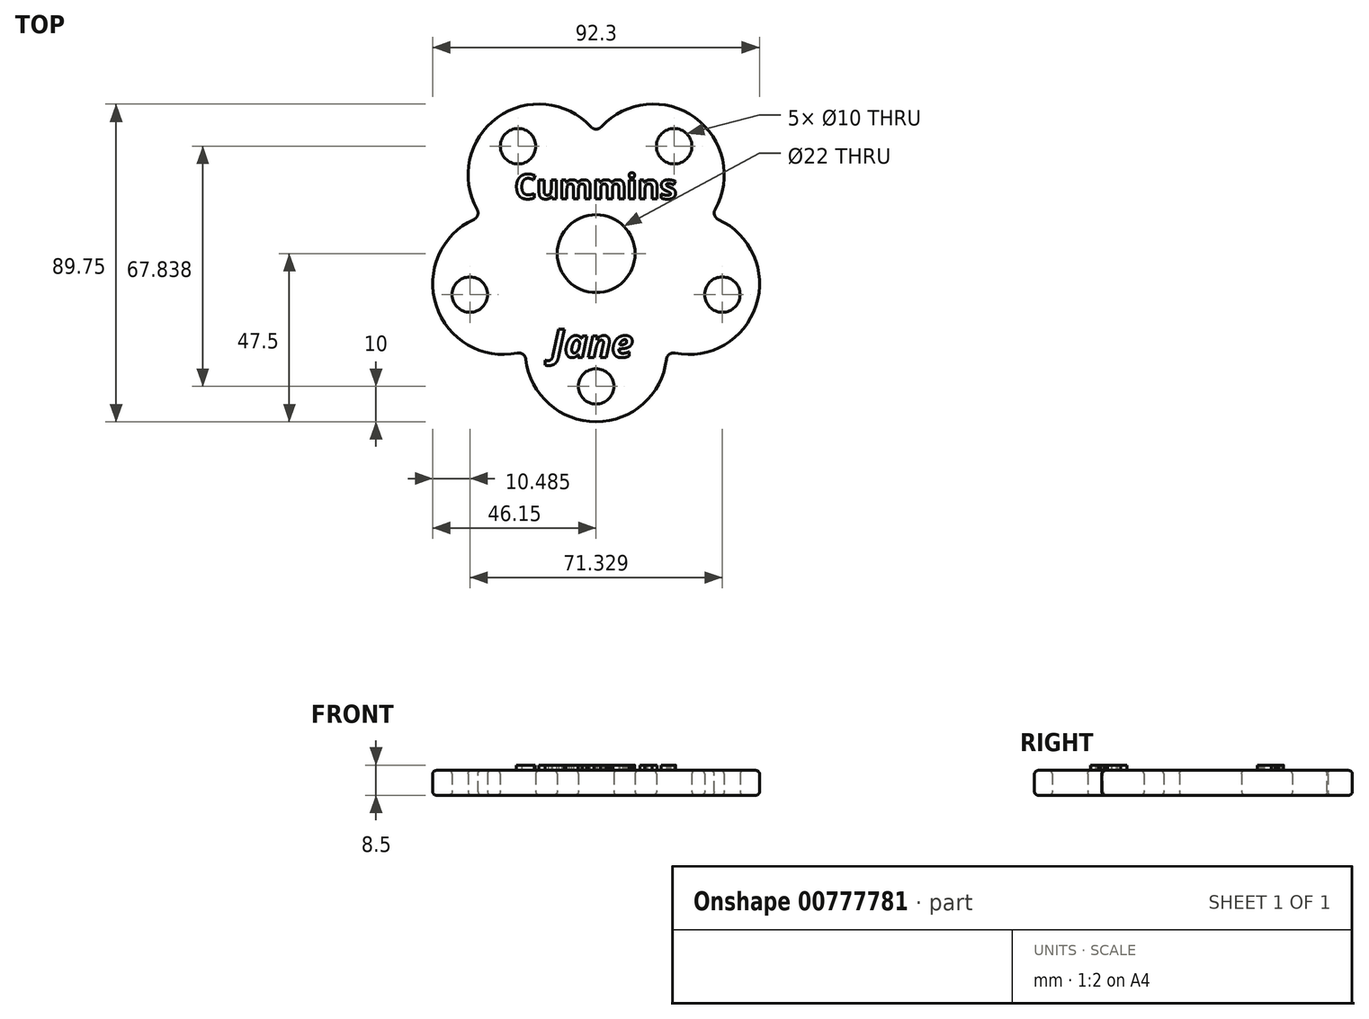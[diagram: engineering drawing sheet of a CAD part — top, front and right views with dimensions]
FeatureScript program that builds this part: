
annotation { "Feature Type Name" : "Feature", "Feature Type Description" : "" }
export const myFeature = defineFeature(function(context is Context, id is Id, definition is map)
    precondition{}
    {
        {
            var Q0;
            Q0=qCreatedBy(makeId("Top.planeOp"),FACE);
            var sketch = newSketch(context, id + "F0", { "sketchPlane" : qUnion([Q0])});
            skCircle(sketch, "E0.cCircle", {"center": v(0, 0) * mm, "radius": 27.5 * mm, "construction": true});
            skPoint(sketch, "E0.0.midPoint", {"position": v(16.16, 22.25) * mm});
            skArc(sketch, "E1", {"start": v(0, 34.03) * mm, "mid": v(-27.92, 38.43) * mm, "end": v(-32.36, 10.51) * mm});
            skArc(sketch, "E2", {"start": v(32.36, 10.51) * mm, "mid": v(27.92, 38.43) * mm, "end": v(0, 34.03) * mm});
            skArc(sketch, "E3", {"start": v(20, -27.53) * mm, "mid": v(45.18, -14.68) * mm, "end": v(32.36, 10.51) * mm});
            skArc(sketch, "E4", {"start": v(-20, -27.53) * mm, "mid": v(0, -47.5) * mm, "end": v(20, -27.53) * mm});
            skArc(sketch, "E5", {"start": v(-32.36, 10.51) * mm, "mid": v(-45.18, -14.68) * mm, "end": v(-20, -27.53) * mm});
            skCircle(sketch, "E6", {"center": v(0, 0) * mm, "radius": 34.03 * mm, "construction": true});
            skCircle(sketch, "E7", {"center": v(0, 0) * mm, "radius": 11 * mm});
            skCircle(sketch, "E8", {"center": v(-22.04, 30.34) * mm, "radius": 5 * mm});
            skCircle(sketch, "E9", {"center": v(22.04, 30.34) * mm, "radius": 5 * mm});
            skCircle(sketch, "E10", {"center": v(35.66, -11.59) * mm, "radius": 5 * mm});
            skCircle(sketch, "E11", {"center": v(0, -37.5) * mm, "radius": 5 * mm});
            skCircle(sketch, "E12", {"center": v(-35.66, -11.59) * mm, "radius": 5 * mm});
            skCircle(sketch, "E13", {"center": v(0, 0) * mm, "radius": 37.5 * mm, "construction": true});
            skLineSegment(sketch, "E14", {"start": v(0, 0) * mm, "end": v(0, 61.86) * mm, "construction": true});
            skLineSegment(sketch, "E15", {"start": v(0, 0) * mm, "end": v(39.94, 54.97) * mm, "construction": true});
            skLineSegment(sketch, "E16", {"start": v(0, 0) * mm, "end": v(78.38, -25.47) * mm, "construction": true});
            skLineSegment(sketch, "E17", {"start": v(0, 0) * mm, "end": v(0, -42.5) * mm, "construction": true});
            skLineSegment(sketch, "E18", {"start": v(0, 0) * mm, "end": v(-69.94, -22.72) * mm, "construction": true});
            skLineSegment(sketch, "E19", {"start": v(0, 0) * mm, "end": v(-36.6, 50.37) * mm, "construction": true});
            skSolve(sketch);
        }
        {
            var Q0;
            Q0=qSketchRegion(id+"F0",true);
            extrude(context, id + "F1", {"entities" : qUnion([Q0]), "depth" : 7 * mm, "offsetDistance" : 25.4 * mm});
        }
        {
            var Q0;
            Q0=makeQuery(id+"F1.opExtrude","SWEPT_EDGE",EDGE,{"disambiguationData":[OSD([sQuery(id+"F0.wireOp",EDGE,"E3"),sQuery(id+"F0.wireOp",EDGE,"E4")])]});
            var Q1;
            Q1=makeQuery(id+"F1.opExtrude","SWEPT_EDGE",EDGE,{"disambiguationData":[OSD([sQuery(id+"F0.wireOp",EDGE,"E2"),sQuery(id+"F0.wireOp",EDGE,"E3")])]});
            var Q2;
            Q2=makeQuery(id+"F1.opExtrude","SWEPT_EDGE",EDGE,{"disambiguationData":[OSD([sQuery(id+"F0.wireOp",EDGE,"E1"),sQuery(id+"F0.wireOp",EDGE,"E2")])]});
            var Q3;
            Q3=makeQuery(id+"F1.opExtrude","SWEPT_EDGE",EDGE,{"disambiguationData":[OSD([sQuery(id+"F0.wireOp",EDGE,"E1"),sQuery(id+"F0.wireOp",EDGE,"E5")])]});
            var Q4;
            Q4=makeQuery(id+"F1.opExtrude","SWEPT_EDGE",EDGE,{"disambiguationData":[OSD([sQuery(id+"F0.wireOp",EDGE,"E4"),sQuery(id+"F0.wireOp",EDGE,"E5")])]});
            fillet(context, id + "F2", {"entities" : qUnion([Q0, Q1, Q2, Q3, Q4]), "radius" : 2 * mm, "tangentPropagation" : true, "allowEdgeOverflow" : false});
        }
        {
            var Q0;
            Q0=makeQuery(id+"F1.opExtrude","CAP_FACE",FACE,{"disambiguationData":[OSD([sQuery(id+"F0.wireOp",EDGE,"E1"),sQuery(id+"F0.wireOp",EDGE,"E2"),sQuery(id+"F0.wireOp",EDGE,"E3"),sQuery(id+"F0.wireOp",EDGE,"E4"),sQuery(id+"F0.wireOp",EDGE,"E5"),sQuery(id+"F0.wireOp",EDGE,"E7"),sQuery(id+"F0.wireOp",EDGE,"E8"),sQuery(id+"F0.wireOp",EDGE,"E9"),sQuery(id+"F0.wireOp",EDGE,"E10"),sQuery(id+"F0.wireOp",EDGE,"E11"),sQuery(id+"F0.wireOp",EDGE,"E12")])],"isStart":false});
            var Q1;
            Q1=makeQuery(id+"F1.opExtrude","CAP_FACE",FACE,{"disambiguationData":[OSD([sQuery(id+"F0.wireOp",EDGE,"E1"),sQuery(id+"F0.wireOp",EDGE,"E2"),sQuery(id+"F0.wireOp",EDGE,"E3"),sQuery(id+"F0.wireOp",EDGE,"E4"),sQuery(id+"F0.wireOp",EDGE,"E5"),sQuery(id+"F0.wireOp",EDGE,"E7"),sQuery(id+"F0.wireOp",EDGE,"E8"),sQuery(id+"F0.wireOp",EDGE,"E9"),sQuery(id+"F0.wireOp",EDGE,"E10"),sQuery(id+"F0.wireOp",EDGE,"E11"),sQuery(id+"F0.wireOp",EDGE,"E12")])],"isStart":true});
            fillet(context, id + "F3", {"entities" : qUnion([Q0, Q1]), "radius" : 1 * mm, "tangentPropagation" : true, "allowEdgeOverflow" : false});
        }
        {
            var Q0;
            Q0=makeQuery(id+"F1.opExtrude","CAP_FACE",FACE,{"disambiguationData":[OSD([sQuery(id+"F0.wireOp",EDGE,"E1"),sQuery(id+"F0.wireOp",EDGE,"E2"),sQuery(id+"F0.wireOp",EDGE,"E3"),sQuery(id+"F0.wireOp",EDGE,"E4"),sQuery(id+"F0.wireOp",EDGE,"E5"),sQuery(id+"F0.wireOp",EDGE,"E7"),sQuery(id+"F0.wireOp",EDGE,"E8"),sQuery(id+"F0.wireOp",EDGE,"E9"),sQuery(id+"F0.wireOp",EDGE,"E10"),sQuery(id+"F0.wireOp",EDGE,"E11"),sQuery(id+"F0.wireOp",EDGE,"E12")])],"isStart":false});
            var sketch = newSketch(context, id + "F4", { "sketchPlane" : qUnion([Q0])});
            skText(sketch, "E20", { "text": "Jane", "fontName": "OpenSans-BoldItalic.ttf"});
            skText(sketch, "E21", { "text": "Cummins", "fontName": "OpenSans-Bold.ttf"});
            const initialGuessF4  = {"E20": [-0.01269, -0.0293, 1, 0, 0.008], "E21": [-0.02306, 0.01547, 1, 0, 0.007]};
            skSetInitialGuess(sketch, initialGuessF4);
            skSolve(sketch);
        }
        {
            var Q0;
            Q0=qSketchRegion(id+"F4",true);
            extrude(context, id + "F5", {"entities" : qUnion([Q0]), "operationType" : NewBodyOperationType.ADD, "depth" : 1.5 * mm, "offsetDistance" : 25 * mm});
        }
    });
